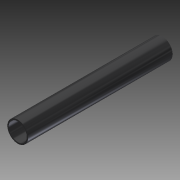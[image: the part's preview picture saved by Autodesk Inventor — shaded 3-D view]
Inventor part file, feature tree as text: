
AUTODESK INVENTOR PART (.ipt)
format: ipt  version: 2013 (Build 170138000, 138)  size: 78,848 bytes
history: native  units: in
note: dims shown in document units (in); Inventor stores cm internally (conversion verified against a paired STEP export)
features: extrude x2, sketch x2
ambient origin geometry x8: Origin, YZ Plane, XZ Plane, XY Plane, X Axis, Y Axis, Z Axis, Center Point
bodies: Solid1 (feature_tree)
feature tree (4):
  extrude  "Extrusion1"  Depth=8.0in TaperAngle=0.0deg
  extrude  "Extrusion3"  Depth=8.0in TaperAngle=0.0deg
  sketch  "Sketch1"  dims[d0=1.15in d1=8.0in d2=0.0in]
  sketch  "Sketch3"  dims[d10=1.0in d11=8.0in d12=0.0in]
